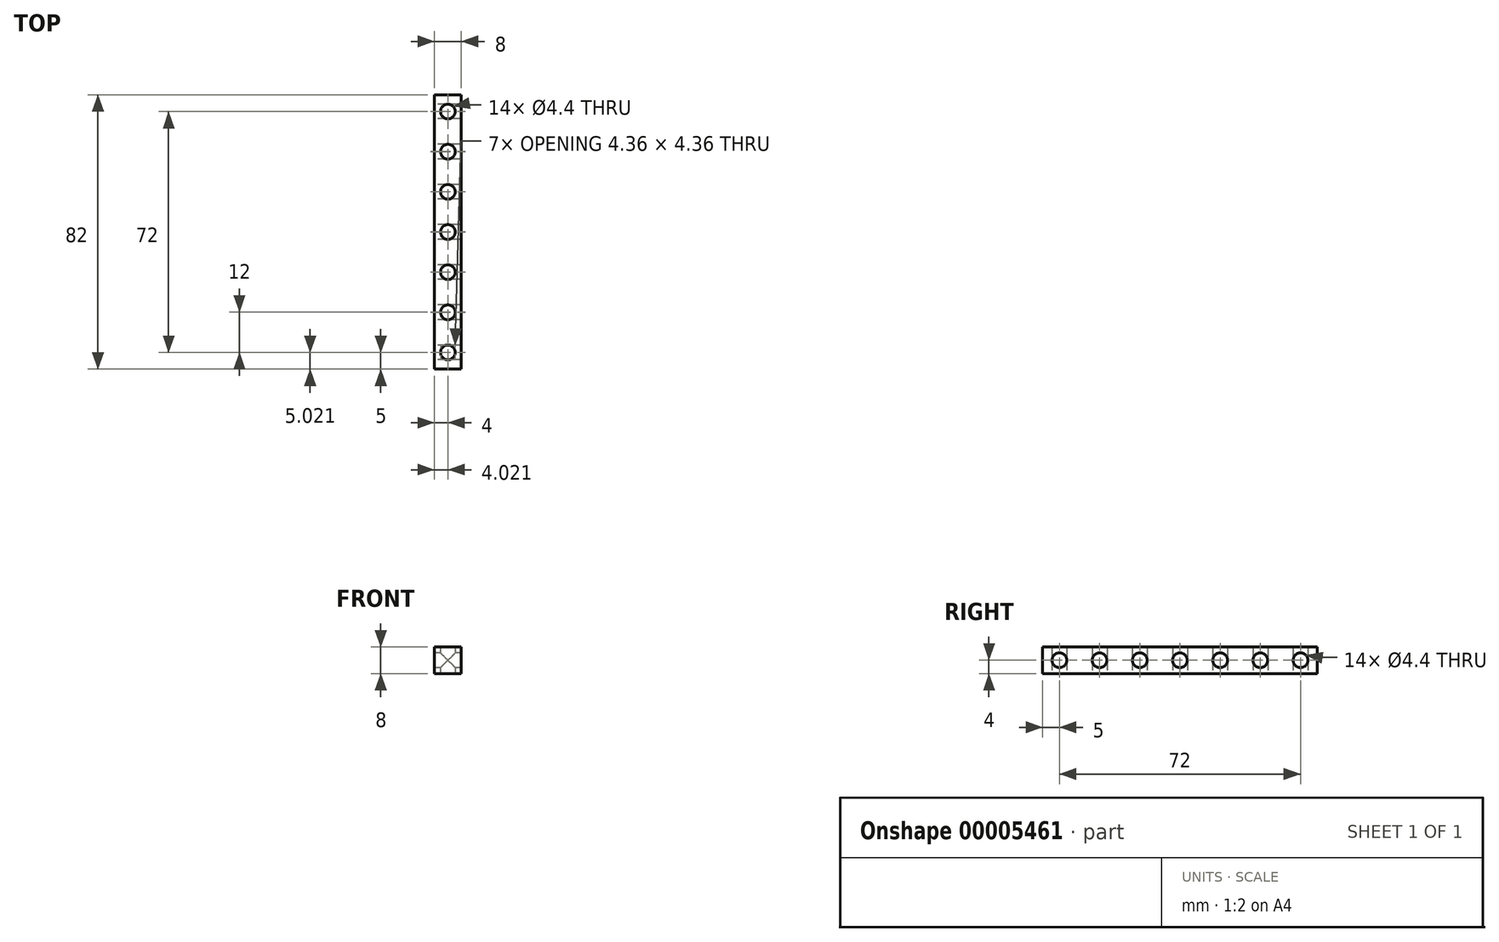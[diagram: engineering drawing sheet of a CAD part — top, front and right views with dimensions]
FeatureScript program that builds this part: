
annotation { "Feature Type Name" : "Feature", "Feature Type Description" : "" }
export const myFeature = defineFeature(function(context is Context, id is Id, definition is map)
    precondition{}
    {
        {
            var Q0;
            Q0=qCreatedBy(makeId("Top.planeOp"),FACE);
            var sketch = newSketch(context, id + "F0", { "sketchPlane" : qUnion([Q0])});
            skLineSegment(sketch, "E0.bottom", {"start": v(0, 0) * mm, "end": v(8, 0) * mm});
            skLineSegment(sketch, "E0.top", {"start": v(0, 82) * mm, "end": v(8, 82) * mm});
            skLineSegment(sketch, "E0.left", {"start": v(0, 0) * mm, "end": v(0, 82) * mm});
            skLineSegment(sketch, "E0.right", {"start": v(8, 0) * mm, "end": v(8, 82) * mm});
            skCircle(sketch, "E1", {"center": v(4, 5) * mm, "radius": 2.2 * mm});
            skPoint(sketch, "E1.centerSnap0", {"position": v(4, 0) * mm});
            skCircle(sketch, "E2.0.1.0", {"center": v(4, 17) * mm, "radius": 2.2 * mm});
            skCircle(sketch, "E2.0.2.0", {"center": v(4, 29) * mm, "radius": 2.2 * mm});
            skCircle(sketch, "E2.0.3.0", {"center": v(4, 41) * mm, "radius": 2.2 * mm});
            skCircle(sketch, "E2.0.4.0", {"center": v(4, 53) * mm, "radius": 2.2 * mm});
            skCircle(sketch, "E2.0.5.0", {"center": v(4, 65) * mm, "radius": 2.2 * mm});
            skCircle(sketch, "E2.0.6.0", {"center": v(4, 77) * mm, "radius": 2.2 * mm});
            skLineSegment(sketch, "E2.direction1", {"start": v(4, 5) * mm, "end": v(29, 5) * mm, "construction": true});
            skLineSegment(sketch, "E2.direction2", {"start": v(4, 5) * mm, "end": v(4, 17) * mm, "construction": true});
            skSolve(sketch);
        }
        {
            var Q0;
            Q0 = qSketchRegion(id + "F0", true);
            extrude(context, id + "F1", {"entities" : qUnion([Q0]), "depth" : 8 * mm, "offsetDistance" : 25 * mm});
        }
        {
            var Q0;
            Q0=makeQuery(id+"F1.opExtrude","SWEPT_FACE",FACE,{"disambiguationData":[OSD([sQuery(id+"F0.wireOp",EDGE,"E0.left")])]});
            var sketch = newSketch(context, id + "F2", { "sketchPlane" : qUnion([Q0])});
            skLineSegment(sketch, "E3.0", {"start": v(-7.2, 8) * mm, "end": v(-2.8, 8) * mm, "construction": true});
            skCircle(sketch, "E4", {"center": v(-5, 4) * mm, "radius": 2.2 * mm});
            skPoint(sketch, "E4.centerSnap0", {"position": v(0, 4) * mm});
            skPoint(sketch, "E4.centerSnap1", {"position": v(-5, 8) * mm});
            skPoint(sketch, "E5", {"position": v(-2.8, 4) * mm});
            skCircle(sketch, "E6.1.0.0", {"center": v(-17, 4) * mm, "radius": 2.2 * mm});
            skCircle(sketch, "E6.2.0.0", {"center": v(-29, 4) * mm, "radius": 2.2 * mm});
            skCircle(sketch, "E6.3.0.0", {"center": v(-41, 4) * mm, "radius": 2.2 * mm});
            skCircle(sketch, "E6.4.0.0", {"center": v(-53, 4) * mm, "radius": 2.2 * mm});
            skCircle(sketch, "E6.5.0.0", {"center": v(-65, 4) * mm, "radius": 2.2 * mm});
            skCircle(sketch, "E6.6.0.0", {"center": v(-77, 4) * mm, "radius": 2.2 * mm});
            skLineSegment(sketch, "E6.direction1", {"start": v(-5, 4) * mm, "end": v(-17, 4) * mm, "construction": true});
            skSolve(sketch);
        }
        {
            var Q0;
            Q0 = qSketchRegion(id + "F2", true);
            extrude(context, id + "F3", {"entities" : qUnion([Q0]), "operationType" : NewBodyOperationType.REMOVE, "endBound" : BoundingType.THROUGH_ALL, "oppositeDirection" : true, "depth" : 25 * mm, "offsetDistance" : 25 * mm});
        }
    });
